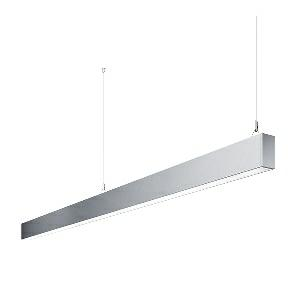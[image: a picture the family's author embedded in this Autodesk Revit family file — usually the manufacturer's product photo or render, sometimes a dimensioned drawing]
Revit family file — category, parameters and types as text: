
# Revit family: idoo_line_-_ilp_6000_vtl_d_end_00806475_eec9
name_source: partatom
category: Lighting Fixtures
units: mm (PartAtom-declared; Revit-internal decimal feet)

## family parameters
Cut with Voids When Loaded = No
Host = Face
Light Source = No
Part Type = Normal
Room Calculation Point = No
Round Connector Dimension = Use Diameter
Shared = No

## types (1)
- IDOO.line - ILP 6000/VTL/D END (1 x LED, 6150 lm, 2700-6500K)
    Apparent Load = 63 VA
    Approval mark = CE
    CIE Flux Codes = 66 91 98 40 100
    Color Rendering = 90-100
    Color Temperature = 2700-6500K
    Control Gear = Electronic ballast
    Default Elevation = 1800 mm
    Description = ILP 6000/VTL/D|Suspended luminaire|light source: LED|connected load: 220-240 V, 50/60 Hz|Power consumption: approx. 63 W|standby: approx. 0,25|luminous flux: 6150 lm|luminous efficacy: 97 lm/W|light distribution: Direct/indirect|direct ratio: approx. 40 %|colour temperature: Cold white, ca. 2700-6500 K|color rendering index (CRI): >= 90|chromaticity tolerance:  3 SDCM|System of protection: IP 40|technology: Continuously dimmable|luminaire body|material: Sectional aluminium|colour: Silver|lamp cover: Acrylic (PMMA), Clear|mains lead: 1,0 m With free stranded wires|Fastening: Steel cable 0.3 - 0.7 m|glare control: Prism aperture|luminance(L65): <= 2700 cd/m|unified glare rating(4H 8H): <=  16|special features: Specified values at approx. 4000 K, DALI Load 1x, Through-wired, up to 18 m on one mains connection, External control required for Dali Device type 8, Flicker-free, Constant luminous flux between 2700 and 6500 K, Constant colour temperature over the whole dimming range, Suitable as emergency lighting, Mechanical and electrical connection of the individual modules without tools|
    Frequency = 50 Hz
    Height = 110 mm
    Lamp = 1 x LED
    Lamp Light Flux = 6150 lm
    Lamp count = 1
    Length = 2250 mm
    Luminous efficacy = 98 lm/W
    Manufacturer = Waldmann
    ModVariant = No
    Model = 00806475
    Mounting Place = Ceiling
    Mounting Type = Pendant
    Number of Poles = 1
    OnlyDefault = Yes
    Power Factor = 1
    Product Name = IDOO.line - ILP 6000/VTL/D END
    Product group = Suspended luminaire
    ProductGroupID = 9
    Protection Class = Protection class I
    Protection Degree = IP 40
    RLX_Detail_Level = 1
    RLX_Emergency_Light_Flux = 0 lm
    RLX_Emergency_Type = 0
    RLX_Emergency_Type_DB = No
    RlxData = <blob elided: 23237 chars, md5=2be038de>
    Socket = socket
    Standby Power = 0 W
    System Light Flux = 6150 lm
    System Power = 63 W
    Type Comments = Product without accessories
    Type Image = 113318000-00692621.jpg
    URL = http://relux.com
    VarID = ---
    Voltage = 230 V
    Voltage Range = 220-240 V
    Weight = 0.00 kg
    Width = 60 mm  [stored 0.19685 ft]

note: [stored X ft] marks values corroborated as IEEE doubles in the binary element streams (Revit-internal decimal feet)

## geometry (parser evidence)
native form markers: Blend x4, Sweep x14
no freeform markers — native parametric forms only
